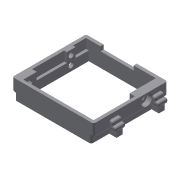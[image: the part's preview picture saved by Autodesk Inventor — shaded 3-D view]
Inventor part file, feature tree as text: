
AUTODESK INVENTOR PART (.ipt)
format: ipt  version: 2017 (Build 210142000, 142)  size: 515,584 bytes
history: native  units: mm
features: extrude x17, sketch x16, fillet x5, other x4, plane x3, shell x2, hole x2, mirror x2
ambient origin geometry x8: Origin, YZ Plane, XZ Plane, XY Plane, X Axis, Y Axis, Z Axis, Center Point
bodies: Solid1 (feature_tree)
feature tree (51):
  plane  "Work Plane1"
  extrude  "Extrusion1"  Depth=7.25mm TaperAngle=0.0deg
  extrude  "Extrusion2"  Depth=2.5mm TaperAngle=0.0deg
  extrude  "Extrusion3"  Depth=3.5mm TaperAngle=0.0deg
  extrude  "Extrusion4"  Depth=1.8mm TaperAngle=0.0deg
  shell  "Shell1"  Thickness=3.5mm
  extrude  "Extrusion5"  Depth=13.0mm
  hole  "Hole1"  [1 undecoded]
  hole  "Hole2"  [1 undecoded]
  extrude  "Extrusion6"  Depth=10.0mm
  extrude  "Extrusion7"  Depth=10.0mm TaperAngle=0.0deg
  extrude  "Extrusion8"  Depth=10.0mm
  shell  "Shell2"  Thickness=10.0mm
  fillet  "Fillet1"  Radius=3.0mm
  fillet  "Fillet3"  Radius=0.8mm
  extrude  "Extrusion9"  Depth=15.0mm
  fillet  "Fillet4"  Radius=9.499635mm
  extrude  "Extrusion10"  Depth=10.0mm
  plane  "Work Plane2"
  plane  "Work Plane3"
  mirror  "Mirror1"
  mirror  "Mirror2"
  extrude  "Estrusione12"  Depth=10.0mm
  sketch  "Schizzo18"
  extrude  "Estrusione15"  Depth=10.0mm
  extrude  "Estrusione13"  Depth=1.0mm
  extrude  "Estrusione16"  Depth=10.0mm TaperAngle=0.0deg
  extrude  "Estrusione17"  Depth=3.0mm
  extrude  "Estrusione14"  Depth=10.0mm
  extrude  "Extrusion11"  Depth=3.0mm
  fillet  "Fillet5"  Radius=5.0mm
  fillet  "Fillet6"  Radius=3.0mm
  sketch  "Sketch1"  dims[d0=-8.25mm d1=7.25mm d2=0.0mm]
  sketch  "Sketch2"  dims[d3=3.875mm d4=0.0mm d5=2.5mm d6=0.0mm]
  sketch  "Sketch3"  dims[d7=2.0mm d8=0.0mm d9=3.5mm d10=0.0mm]
  sketch  "Sketch5"  dims[d11=1.8mm d12=3.5mm d13=0.0mm]
  sketch  "Sketch6"  dims[d14=3.0mm d15=6.0mm d16=6.0mm d17=2.7mm d18=90.0deg d19=8.0mm d20=20.594885mm]
  sketch  "Sketch7"  dims[d21=3.0mm d22=6.0mm d23=6.0mm d24=2.7mm d25=90.0deg d26=8.0mm d27=20.594885mm d28=3.5mm d29=0.0mm]
  sketch  "Sketch10"  dims[d30=3.5mm d31=0.0mm d32=13.0mm]
  sketch  "Sketch12"  dims[d33=3.5mm d34=0.0mm d35=2.5mm]
  sketch  "Sketch13"  dims[d36=2.0mm d37=4.5mm d40=10.0mm d41=0.0mm]
  sketch  "Sketch14"  dims[d42=1.0mm d43=0.5mm d44=10.0mm d45=0.0mm d46=0.45mm d47=10.0mm d48=0.0mm d49=3.0mm d50=0.8mm d51=15.0mm d52=9.499635mm d53=10.740057mm d54=15.551351mm d57=0.8mm d58=1.0mm d59=2.0mm d60=10.0mm d61=0.0mm d62=3.0mm d63=10.0mm d64=3.0mm d65=5.0mm d66=3.0mm d67=10.0mm d68=0.0mm d69=37.2mm d70=3.0mm d71=15.0mm d72=10.0mm d73=19.0mm d74=2.5mm d75=10.0mm d76=0.0mm d77=5.0mm d78=7.5mm d79=10.0mm d80=0.0mm d81=5.0mm d82=0.0mm d83=5.0mm d84=0.0mm]
  sketch  "Schizzo15"
  other  "Linea chiusa proiettata1"
  sketch  "Schizzo16"
  sketch  "Schizzo17"
  sketch  "Schizzo19"
  other  "Linea chiusa proiettata2"
  sketch  "Schizzo20"
  other  "Linea chiusa proiettata3"
  other  "Linea chiusa proiettata4"
note: 2 required parameter values undecoded (feature->parameter linkage not recoverable at this tier; creation-order binding heuristic only, values carry confidence <= 0.55)
